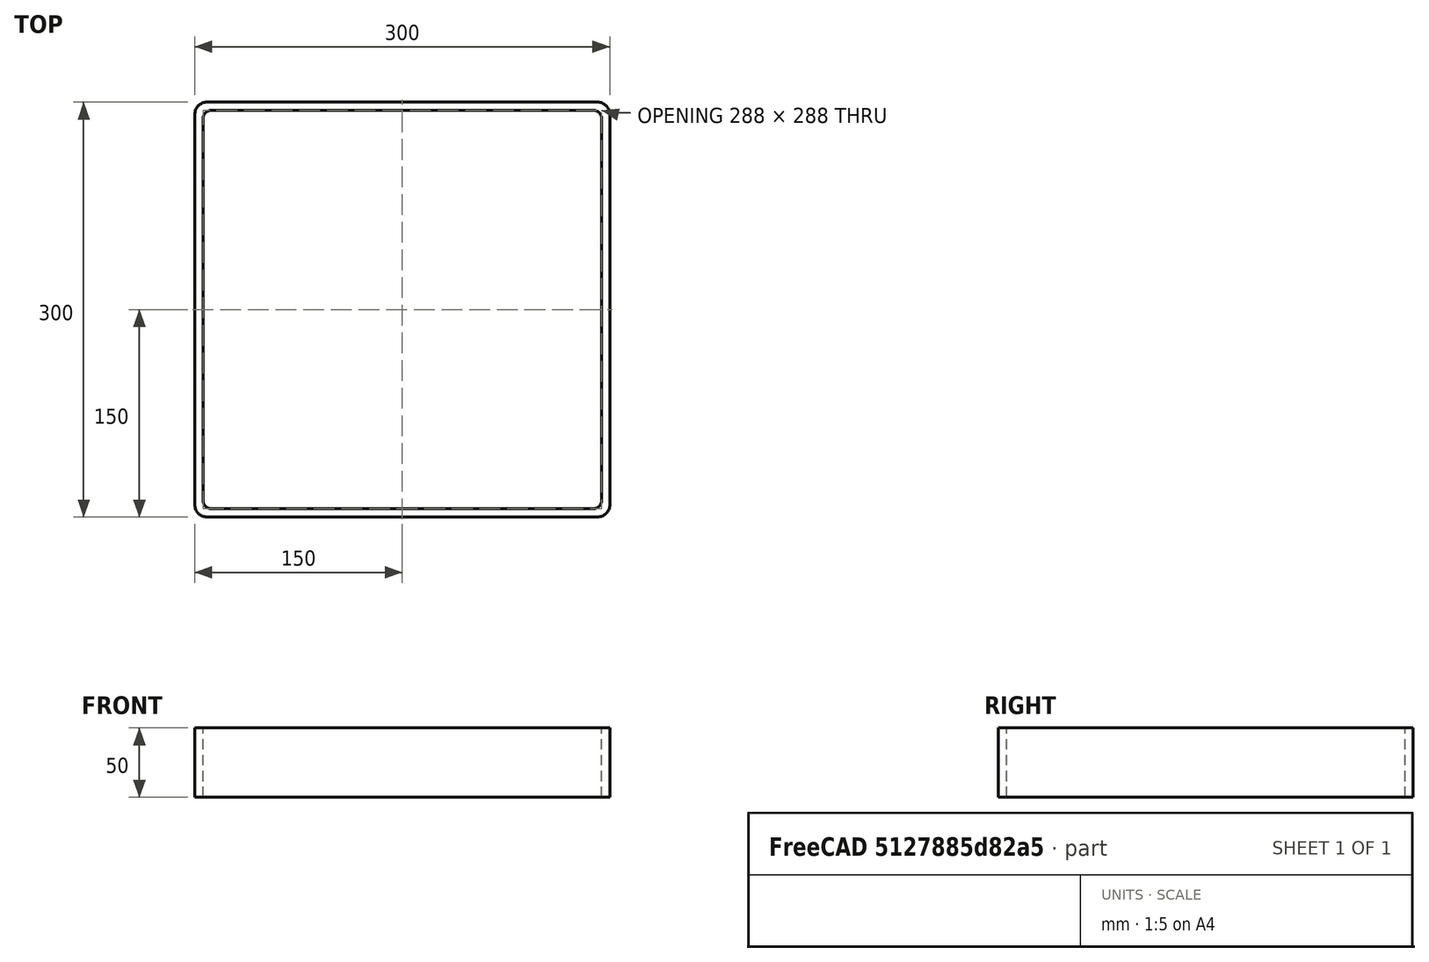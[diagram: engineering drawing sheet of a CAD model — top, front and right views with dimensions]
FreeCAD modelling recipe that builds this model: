
FCSTD DOCUMENT  (FreeCAD 0.15R4671 (Git))
Label: Square hollow section 300x300x6 EN10219 S235JRH
License: All rights reserved
LicenseURL: http://en.wikipedia.org/wiki/All_rights_reserved
objects: Sketcher::SketchObject×1, Part::Extrusion×1
note: 2 computed .brp shape members not serialized (recipe doc carries the construction recipe); baked Part::Feature solids carry a one-line shape summary decoded from their .brp

FEATURE [Sketcher::SketchObject] Sketch
  sketch-geometry (16):
    g0: LineSegment StartX=-138 StartY=144 StartZ=0 EndX=138 EndY=144 EndZ=0
    g1: LineSegment StartX=144 StartY=138 StartZ=0 EndX=144 EndY=-138 EndZ=0
    g2: LineSegment StartX=138 StartY=-144 StartZ=0 EndX=-138 EndY=-144 EndZ=0
    g3: LineSegment StartX=-144 StartY=-138 StartZ=0 EndX=-144 EndY=138 EndZ=0
    g4: LineSegment StartX=-141 StartY=150 StartZ=0 EndX=141 EndY=150 EndZ=0
    g5: LineSegment StartX=150 StartY=141 StartZ=0 EndX=150 EndY=-141 EndZ=0
    g6: LineSegment StartX=141 StartY=-150 StartZ=0 EndX=-141 EndY=-150 EndZ=0
    g7: LineSegment StartX=-150 StartY=-141 StartZ=0 EndX=-150 EndY=141 EndZ=0
    g8: ArcOfCircle CenterX=-138 CenterY=138 CenterZ=0 NormalX=0 NormalY=0 NormalZ=1 Radius=6 StartAngle=1.5708 EndAngle=3.14159
    g9: ArcOfCircle CenterX=138 CenterY=138 CenterZ=0 NormalX=0 NormalY=0 NormalZ=1 Radius=6 StartAngle=0 EndAngle=1.5708
    g10: ArcOfCircle CenterX=138 CenterY=-138 CenterZ=0 NormalX=0 NormalY=0 NormalZ=1 Radius=6 StartAngle=4.71239 EndAngle=6.28319
    g11: ArcOfCircle CenterX=-138 CenterY=-138 CenterZ=0 NormalX=0 NormalY=0 NormalZ=1 Radius=6 StartAngle=3.14159 EndAngle=4.71239
    g12: ArcOfCircle CenterX=141 CenterY=141 CenterZ=0 NormalX=0 NormalY=0 NormalZ=1 Radius=9 StartAngle=0 EndAngle=1.5708
    g13: ArcOfCircle CenterX=141 CenterY=-141 CenterZ=0 NormalX=0 NormalY=0 NormalZ=1 Radius=9 StartAngle=4.71239 EndAngle=6.28319
    g14: ArcOfCircle CenterX=-141 CenterY=-141 CenterZ=0 NormalX=0 NormalY=0 NormalZ=1 Radius=9 StartAngle=3.14159 EndAngle=4.71239
    g15: ArcOfCircle CenterX=-141 CenterY=141 CenterZ=0 NormalX=0 NormalY=0 NormalZ=1 Radius=9 StartAngle=1.5708 EndAngle=3.14159
  constraints (36):
    c: Horizontal(g2)
    c: Vertical(g3)
    c: Horizontal(g6)
    c: Vertical(g7)
    c: Tangent(g3,g8) = 1.5708
    c: Tangent(g0,g8) = 1.5708
    c: Tangent(g0,g9) = 1.5708
    c: Tangent(g1,g9) = 1.5708
    c: Tangent(g1,g10) = 1.5708
    c: Tangent(g2,g10) = 1.5708
    c: Tangent(g2,g11) = 1.5708
    c: Tangent(g3,g11) = 1.5708
    c: Tangent(g4,g12) = 1.5708
    c: Tangent(g5,g12) = 1.5708
    c: Tangent(g5,g13) = 1.5708
    c: Tangent(g6,g13) = 1.5708
    c: Tangent(g6,g14) = 1.5708
    c: Tangent(g7,g14) = 1.5708
    c: Tangent(g7,g15) = 1.5708
    c: Tangent(g4,g15) = 1.5708
    c: Equal(g9,g8)
    c: Equal(g9,g11)
    c: Equal(g9,g10)
    c: Equal(g12,g15)
    c: Equal(g12,g14)
    c: Equal(g12,g13)
    c: Symmetric(g4,g6,g-1)
    c: Symmetric(g7,g5,g-2)
    c: DistanceY(g4,g6) = -300
    c: DistanceX(g7,g5) = 300
    c: Symmetric(g3,g1,g-2)
    c: Symmetric(g0,g2,g-1)
    c: DistanceY(g0,g4) = 6
    c: DistanceX(g5,g1) = -6
    c: Radius(g9) = 6
    c: Radius(g12) = 9
FEATURE [Part::Extrusion] Extrude  label="Square hollow section 300x300x6 EN10219 S235JRH"
  Base = -> Sketch
  Dir = (0,0,50)
  Solid = true
